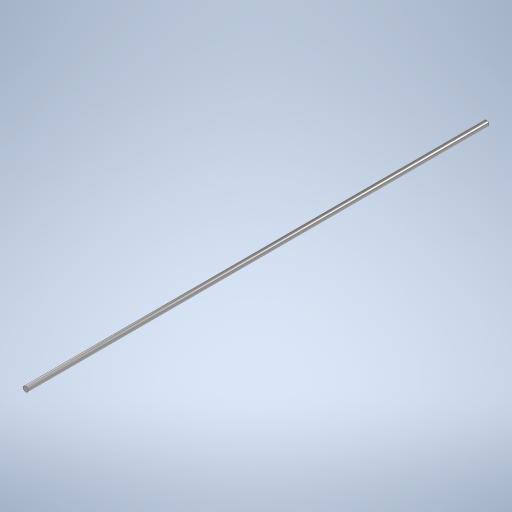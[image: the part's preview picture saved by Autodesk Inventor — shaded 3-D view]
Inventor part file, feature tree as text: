
AUTODESK INVENTOR PART (.ipt)
format: ipt  version: 2023.2 (Build 272271000, 271)  size: 242,688 bytes
history: native  units: mm
features: extrude x1, sketch x1
ambient origin geometry x8: Origin, YZ Plane, XZ Plane, XY Plane, X Axis, Y Axis, Z Axis, Center Point
bodies: Solid1 (feature_tree)
feature tree (2):
  extrude  "Extrusion1"  Depth=700.0mm TaperAngle=0.0deg
  sketch  "Sketch1"  dims[d0=8.0mm d1=700.0mm d2=0.0mm]
